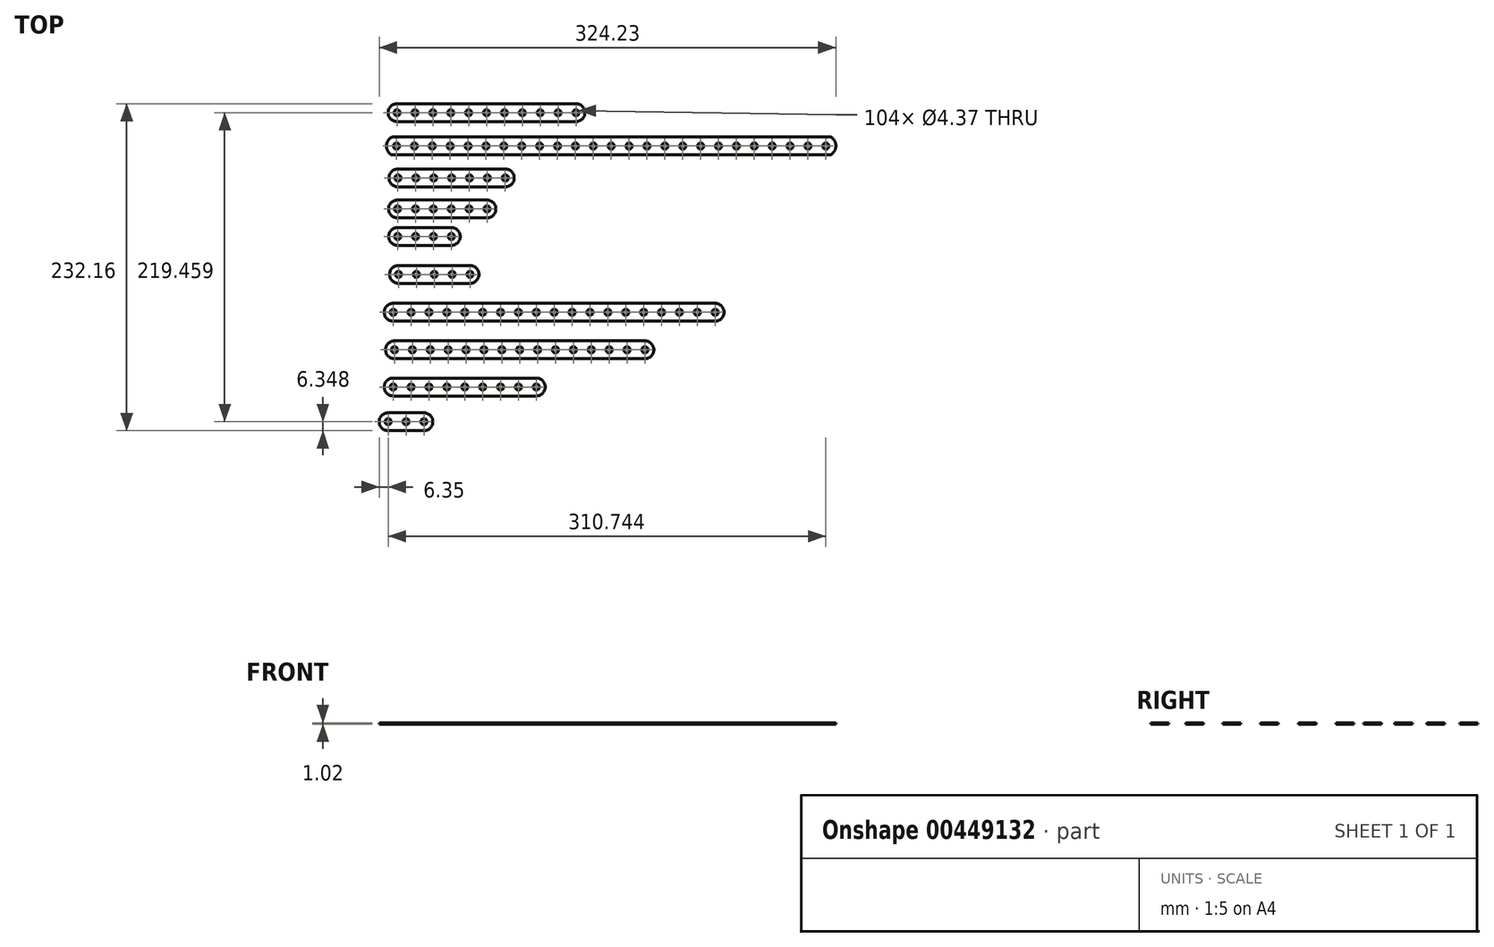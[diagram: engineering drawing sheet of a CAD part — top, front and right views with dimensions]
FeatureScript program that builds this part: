
annotation { "Feature Type Name" : "Feature", "Feature Type Description" : "" }
export const myFeature = defineFeature(function(context is Context, id is Id, definition is map)
    precondition{}
    {
        {
            var Q0;
            Q0=qCreatedBy(makeId("Top.planeOp"),FACE);
            var sketch = newSketch(context, id + "F0", { "sketchPlane" : qUnion([Q0])});
            skLineSegment(sketch, "E0", {"start": v(2.68, 70.57) * mm, "end": v(314.2, 70.57) * mm});
            skLineSegment(sketch, "E1", {"start": v(2.68, 57.87) * mm, "end": v(313.8, 57.87) * mm});
            skPoint(sketch, "E2", {"position": v(5.94, 71.36) * mm});
            skPoint(sketch, "E3", {"position": v(6.08, 56.78) * mm});
            skPoint(sketch, "E4", {"position": v(5.94, 64.22) * mm});
            skArc(sketch, "E5", {"start": v(2.68, 70.57) * mm, "mid": v(-1.2, 64.22) * mm, "end": v(2.68, 57.87) * mm});
            skPoint(sketch, "E6.orphan", {"position": v(0, 70.57) * mm});
            skPoint(sketch, "E7.orphan", {"position": v(5.94, 57.08) * mm});
            skPoint(sketch, "E8.orphan", {"position": v(0, 57.87) * mm});
            skArc(sketch, "E9", {"start": v(314.2, 70.57) * mm, "mid": v(317.88, 64.1) * mm, "end": v(313.8, 57.87) * mm});
            skPoint(sketch, "E10.orphan", {"position": v(310.74, 71.46) * mm});
            skPoint(sketch, "E11.orphan", {"position": v(310.74, 57.18) * mm});
            skCircle(sketch, "E12", {"center": v(5.94, 64.22) * mm, "radius": 2.18 * mm});
            skCircle(sketch, "E13.1.0.0", {"center": v(18.64, 64.22) * mm, "radius": 2.18 * mm});
            skCircle(sketch, "E13.2.0.0", {"center": v(31.34, 64.22) * mm, "radius": 2.18 * mm});
            skLineSegment(sketch, "E13.direction1", {"start": v(5.94, 64.22) * mm, "end": v(18.64, 64.22) * mm, "construction": true});
            skCircle(sketch, "E14.0.3.0", {"center": v(44.04, 64.22) * mm, "radius": 2.18 * mm});
            skCircle(sketch, "E14.0.4.0", {"center": v(56.74, 64.22) * mm, "radius": 2.18 * mm});
            skCircle(sketch, "E14.0.5.0", {"center": v(69.44, 64.22) * mm, "radius": 2.18 * mm});
            skCircle(sketch, "E14.0.6.0", {"center": v(82.14, 64.22) * mm, "radius": 2.18 * mm});
            skCircle(sketch, "E14.0.7.0", {"center": v(94.84, 64.22) * mm, "radius": 2.18 * mm});
            skCircle(sketch, "E14.0.8.0", {"center": v(107.54, 64.22) * mm, "radius": 2.18 * mm});
            skCircle(sketch, "E14.0.9.0", {"center": v(120.24, 64.22) * mm, "radius": 2.18 * mm});
            skCircle(sketch, "E14.0.10.0", {"center": v(132.94, 64.22) * mm, "radius": 2.18 * mm});
            skCircle(sketch, "E14.0.11.0", {"center": v(145.64, 64.22) * mm, "radius": 2.18 * mm});
            skCircle(sketch, "E14.0.12.0", {"center": v(158.34, 64.22) * mm, "radius": 2.18 * mm});
            skCircle(sketch, "E14.0.13.0", {"center": v(171.04, 64.22) * mm, "radius": 2.18 * mm});
            skCircle(sketch, "E14.0.14.0", {"center": v(183.74, 64.22) * mm, "radius": 2.18 * mm});
            skCircle(sketch, "E14.0.15.0", {"center": v(196.44, 64.22) * mm, "radius": 2.18 * mm});
            skCircle(sketch, "E14.0.16.0", {"center": v(209.14, 64.22) * mm, "radius": 2.18 * mm});
            skCircle(sketch, "E14.0.17.0", {"center": v(221.84, 64.22) * mm, "radius": 2.18 * mm});
            skCircle(sketch, "E14.0.18.0", {"center": v(234.54, 64.22) * mm, "radius": 2.18 * mm});
            skCircle(sketch, "E14.0.19.0", {"center": v(247.24, 64.22) * mm, "radius": 2.18 * mm});
            skCircle(sketch, "E14.0.20.0", {"center": v(259.94, 64.22) * mm, "radius": 2.18 * mm});
            skCircle(sketch, "E14.0.21.0", {"center": v(272.64, 64.22) * mm, "radius": 2.18 * mm});
            skCircle(sketch, "E14.0.22.0", {"center": v(285.34, 64.22) * mm, "radius": 2.18 * mm});
            skCircle(sketch, "E14.0.23.0", {"center": v(298.04, 64.22) * mm, "radius": 2.18 * mm});
            skCircle(sketch, "E14.0.24.0", {"center": v(310.74, 64.22) * mm, "radius": 2.18 * mm});
            skSolve(sketch);
        }
        {
            var Q0;
            Q0 = qSketchRegion(id + "F0", true);
            extrude(context, id + "F1", {"entities" : qUnion([Q0]), "depth" : 1.02 * mm});
        }
        {
            var Q0;
            Q0=qCreatedBy(makeId("Top.planeOp"),FACE);
            var sketch = newSketch(context, id + "F2", { "sketchPlane" : qUnion([Q0])});
            skLineSegment(sketch, "E15", {"start": v(6.35, 94.24) * mm, "end": v(133.35, 94.24) * mm});
            skLineSegment(sketch, "E16", {"start": v(6.35, 81.54) * mm, "end": v(133.35, 81.54) * mm});
            skArc(sketch, "E17", {"start": v(6.35, 94.24) * mm, "mid": v(0, 87.89) * mm, "end": v(6.35, 81.54) * mm});
            skArc(sketch, "E18", {"start": v(133.35, 94.24) * mm, "mid": v(139.7, 87.89) * mm, "end": v(133.35, 81.54) * mm});
            skCircle(sketch, "E19", {"center": v(6.35, 87.89) * mm, "radius": 2.18 * mm});
            skCircle(sketch, "E20.1.0.0", {"center": v(19.05, 87.89) * mm, "radius": 2.18 * mm});
            skCircle(sketch, "E20.2.0.0", {"center": v(31.75, 87.89) * mm, "radius": 2.18 * mm});
            skLineSegment(sketch, "E20.direction1", {"start": v(6.35, 87.89) * mm, "end": v(19.05, 87.89) * mm, "construction": true});
            skCircle(sketch, "E21.0.3.0", {"center": v(44.45, 87.89) * mm, "radius": 2.18 * mm});
            skCircle(sketch, "E21.0.4.0", {"center": v(57.15, 87.89) * mm, "radius": 2.18 * mm});
            skCircle(sketch, "E21.0.5.0", {"center": v(69.85, 87.89) * mm, "radius": 2.18 * mm});
            skCircle(sketch, "E21.0.6.0", {"center": v(82.55, 87.89) * mm, "radius": 2.18 * mm});
            skCircle(sketch, "E21.0.7.0", {"center": v(95.25, 87.89) * mm, "radius": 2.18 * mm});
            skCircle(sketch, "E21.0.8.0", {"center": v(107.95, 87.89) * mm, "radius": 2.18 * mm});
            skCircle(sketch, "E21.0.9.0", {"center": v(120.65, 87.89) * mm, "radius": 2.18 * mm});
            skCircle(sketch, "E21.0.10.0", {"center": v(133.35, 87.89) * mm, "radius": 2.18 * mm});
            skSolve(sketch);
        }
        {
            var Q0;
            Q0 = qSketchRegion(id + "F2", true);
            extrude(context, id + "F3", {"entities" : qUnion([Q0]), "depth" : 1.02 * mm});
        }
        {
            var Q0;
            Q0=qCreatedBy(makeId("Top.planeOp"),FACE);
            var sketch = newSketch(context, id + "F4", { "sketchPlane" : qUnion([Q0])});
            skLineSegment(sketch, "E22", {"start": v(6.95, 47.9) * mm, "end": v(83.15, 47.9) * mm});
            skLineSegment(sketch, "E23", {"start": v(6.95, 35.2) * mm, "end": v(83.15, 35.2) * mm});
            skArc(sketch, "E24", {"start": v(6.95, 47.9) * mm, "mid": v(0.6, 41.55) * mm, "end": v(6.95, 35.2) * mm});
            skArc(sketch, "E25", {"start": v(83.15, 47.9) * mm, "mid": v(89.5, 41.55) * mm, "end": v(83.15, 35.2) * mm});
            skCircle(sketch, "E26", {"center": v(6.95, 41.55) * mm, "radius": 2.18 * mm});
            skCircle(sketch, "E27.1.0.0", {"center": v(19.65, 41.55) * mm, "radius": 2.18 * mm});
            skCircle(sketch, "E27.2.0.0", {"center": v(32.35, 41.55) * mm, "radius": 2.18 * mm});
            skLineSegment(sketch, "E27.direction1", {"start": v(6.95, 41.55) * mm, "end": v(19.65, 41.55) * mm, "construction": true});
            skCircle(sketch, "E28.0.3.0", {"center": v(45.05, 41.55) * mm, "radius": 2.18 * mm});
            skCircle(sketch, "E28.0.4.0", {"center": v(57.75, 41.55) * mm, "radius": 2.18 * mm});
            skCircle(sketch, "E28.0.5.0", {"center": v(70.45, 41.55) * mm, "radius": 2.18 * mm});
            skCircle(sketch, "E28.0.6.0", {"center": v(83.15, 41.55) * mm, "radius": 2.18 * mm});
            skSolve(sketch);
        }
        {
            var Q0;
            Q0 = qSketchRegion(id + "F4", true);
            extrude(context, id + "F5", {"entities" : qUnion([Q0]), "depth" : 1.02 * mm});
        }
        {
            var Q0;
            Q0=qCreatedBy(makeId("Top.planeOp"),FACE);
            var sketch = newSketch(context, id + "F6", { "sketchPlane" : qUnion([Q0])});
            skLineSegment(sketch, "E29", {"start": v(6.67, 25.9) * mm, "end": v(70.17, 25.9) * mm});
            skLineSegment(sketch, "E30", {"start": v(6.67, 13.2) * mm, "end": v(70.17, 13.2) * mm});
            skArc(sketch, "E31", {"start": v(6.67, 25.9) * mm, "mid": v(0.32, 19.56) * mm, "end": v(6.67, 13.2) * mm});
            skArc(sketch, "E32", {"start": v(70.17, 25.9) * mm, "mid": v(76.52, 19.56) * mm, "end": v(70.17, 13.2) * mm});
            skCircle(sketch, "E33", {"center": v(6.67, 19.56) * mm, "radius": 2.18 * mm});
            skCircle(sketch, "E34.1.0.0", {"center": v(19.37, 19.56) * mm, "radius": 2.18 * mm});
            skCircle(sketch, "E34.2.0.0", {"center": v(32.07, 19.56) * mm, "radius": 2.18 * mm});
            skLineSegment(sketch, "E34.direction1", {"start": v(6.67, 19.56) * mm, "end": v(19.37, 19.56) * mm, "construction": true});
            skCircle(sketch, "E35.0.3.0", {"center": v(44.77, 19.56) * mm, "radius": 2.18 * mm});
            skCircle(sketch, "E35.0.4.0", {"center": v(57.47, 19.56) * mm, "radius": 2.18 * mm});
            skCircle(sketch, "E35.0.5.0", {"center": v(70.17, 19.56) * mm, "radius": 2.18 * mm});
            skSolve(sketch);
        }
        {
            var Q0;
            Q0 = qSketchRegion(id + "F6", true);
            extrude(context, id + "F7", {"entities" : qUnion([Q0]), "depth" : 1.02 * mm});
        }
        {
            var Q0;
            Q0=qCreatedBy(makeId("Top.planeOp"),FACE);
            var sketch = newSketch(context, id + "F8", { "sketchPlane" : qUnion([Q0])});
            skLineSegment(sketch, "E36", {"start": v(7.36, -20.6) * mm, "end": v(58.16, -20.6) * mm});
            skLineSegment(sketch, "E37", {"start": v(7.36, -33.3) * mm, "end": v(58.16, -33.3) * mm});
            skArc(sketch, "E38", {"start": v(7.36, -20.6) * mm, "mid": v(1, -26.96) * mm, "end": v(7.36, -33.3) * mm});
            skArc(sketch, "E39", {"start": v(58.16, -20.6) * mm, "mid": v(64.5, -26.96) * mm, "end": v(58.16, -33.3) * mm});
            skCircle(sketch, "E40", {"center": v(7.36, -26.96) * mm, "radius": 2.18 * mm});
            skCircle(sketch, "E41.1.0.0", {"center": v(20.06, -26.96) * mm, "radius": 2.18 * mm});
            skCircle(sketch, "E41.2.0.0", {"center": v(32.76, -26.96) * mm, "radius": 2.18 * mm});
            skLineSegment(sketch, "E41.direction1", {"start": v(7.36, -26.96) * mm, "end": v(20.06, -26.96) * mm, "construction": true});
            skCircle(sketch, "E42.0.3.0", {"center": v(45.46, -26.96) * mm, "radius": 2.18 * mm});
            skCircle(sketch, "E42.0.4.0", {"center": v(58.16, -26.96) * mm, "radius": 2.18 * mm});
            skSolve(sketch);
        }
        {
            var Q0;
            Q0 = qSketchRegion(id + "F8", true);
            extrude(context, id + "F9", {"entities" : qUnion([Q0]), "depth" : 1.02 * mm});
        }
        {
            var Q0;
            Q0=qCreatedBy(makeId("Top.planeOp"),FACE);
            var sketch = newSketch(context, id + "F10", { "sketchPlane" : qUnion([Q0])});
            skLineSegment(sketch, "E43", {"start": v(6.76, 6.32) * mm, "end": v(44.86, 6.32) * mm});
            skLineSegment(sketch, "E44", {"start": v(6.76, -6.38) * mm, "end": v(44.86, -6.38) * mm});
            skArc(sketch, "E45", {"start": v(6.76, 6.32) * mm, "mid": v(0.41, -0.03) * mm, "end": v(6.76, -6.38) * mm});
            skArc(sketch, "E46", {"start": v(44.86, 6.32) * mm, "mid": v(51.21, -0.03) * mm, "end": v(44.86, -6.38) * mm});
            skCircle(sketch, "E47", {"center": v(6.76, -0.03) * mm, "radius": 2.18 * mm});
            skCircle(sketch, "E48.1.0.0", {"center": v(19.46, -0.03) * mm, "radius": 2.18 * mm});
            skCircle(sketch, "E48.2.0.0", {"center": v(32.16, -0.03) * mm, "radius": 2.18 * mm});
            skLineSegment(sketch, "E48.direction1", {"start": v(6.76, -0.03) * mm, "end": v(19.46, -0.03) * mm, "construction": true});
            skCircle(sketch, "E49.0.3.0", {"center": v(44.86, -0.03) * mm, "radius": 2.18 * mm});
            skSolve(sketch);
        }
        {
            var Q0;
            Q0 = qSketchRegion(id + "F10", true);
            extrude(context, id + "F11", {"entities" : qUnion([Q0]), "depth" : 1.02 * mm});
        }
        {
            var Q0;
            Q0=qCreatedBy(makeId("Top.planeOp"),FACE);
            var sketch = newSketch(context, id + "F12", { "sketchPlane" : qUnion([Q0])});
            skLineSegment(sketch, "E50", {"start": v(3.57, -47.5) * mm, "end": v(232.17, -47.5) * mm});
            skLineSegment(sketch, "E51", {"start": v(3.57, -60.2) * mm, "end": v(232.17, -60.2) * mm});
            skArc(sketch, "E52", {"start": v(3.57, -47.5) * mm, "mid": v(-2.78, -53.85) * mm, "end": v(3.57, -60.2) * mm});
            skArc(sketch, "E53", {"start": v(232.17, -47.5) * mm, "mid": v(238.52, -53.85) * mm, "end": v(232.17, -60.2) * mm});
            skCircle(sketch, "E54", {"center": v(3.57, -53.85) * mm, "radius": 2.18 * mm});
            skCircle(sketch, "E55.1.0.0", {"center": v(16.27, -53.85) * mm, "radius": 2.18 * mm});
            skCircle(sketch, "E55.2.0.0", {"center": v(28.97, -53.85) * mm, "radius": 2.18 * mm});
            skLineSegment(sketch, "E55.direction1", {"start": v(3.57, -53.85) * mm, "end": v(16.27, -53.85) * mm, "construction": true});
            skCircle(sketch, "E56.0.3.0", {"center": v(41.67, -53.85) * mm, "radius": 2.18 * mm});
            skCircle(sketch, "E56.0.4.0", {"center": v(54.37, -53.85) * mm, "radius": 2.18 * mm});
            skCircle(sketch, "E56.0.5.0", {"center": v(67.07, -53.85) * mm, "radius": 2.18 * mm});
            skCircle(sketch, "E56.0.6.0", {"center": v(79.77, -53.85) * mm, "radius": 2.18 * mm});
            skCircle(sketch, "E56.0.7.0", {"center": v(92.47, -53.85) * mm, "radius": 2.18 * mm});
            skCircle(sketch, "E56.0.8.0", {"center": v(105.17, -53.85) * mm, "radius": 2.18 * mm});
            skCircle(sketch, "E56.0.9.0", {"center": v(117.87, -53.85) * mm, "radius": 2.18 * mm});
            skCircle(sketch, "E56.0.10.0", {"center": v(130.57, -53.85) * mm, "radius": 2.18 * mm});
            skCircle(sketch, "E57.0.11.0", {"center": v(143.27, -53.85) * mm, "radius": 2.18 * mm});
            skCircle(sketch, "E57.0.12.0", {"center": v(155.97, -53.85) * mm, "radius": 2.18 * mm});
            skCircle(sketch, "E57.0.13.0", {"center": v(168.67, -53.85) * mm, "radius": 2.18 * mm});
            skCircle(sketch, "E57.0.14.0", {"center": v(181.37, -53.85) * mm, "radius": 2.18 * mm});
            skCircle(sketch, "E57.0.15.0", {"center": v(194.07, -53.85) * mm, "radius": 2.18 * mm});
            skCircle(sketch, "E57.0.16.0", {"center": v(206.77, -53.85) * mm, "radius": 2.18 * mm});
            skCircle(sketch, "E57.0.17.0", {"center": v(219.47, -53.85) * mm, "radius": 2.18 * mm});
            skCircle(sketch, "E57.0.18.0", {"center": v(232.17, -53.85) * mm, "radius": 2.18 * mm});
            skSolve(sketch);
        }
        {
            var Q0;
            Q0 = qSketchRegion(id + "F12", true);
            extrude(context, id + "F13", {"entities" : qUnion([Q0]), "depth" : 1.02 * mm});
        }
        {
            var Q0;
            Q0=qCreatedBy(makeId("Top.planeOp"),FACE);
            var sketch = newSketch(context, id + "F14", { "sketchPlane" : qUnion([Q0])});
            skLineSegment(sketch, "E58", {"start": v(4.5, -74.17) * mm, "end": v(182.3, -74.17) * mm});
            skLineSegment(sketch, "E59", {"start": v(4.5, -86.87) * mm, "end": v(182.3, -86.87) * mm});
            skArc(sketch, "E60", {"start": v(4.5, -74.17) * mm, "mid": v(-1.85, -80.52) * mm, "end": v(4.5, -86.87) * mm});
            skArc(sketch, "E61", {"start": v(182.3, -74.17) * mm, "mid": v(188.65, -80.52) * mm, "end": v(182.3, -86.87) * mm});
            skCircle(sketch, "E62", {"center": v(4.5, -80.52) * mm, "radius": 2.18 * mm});
            skCircle(sketch, "E63.1.0.0", {"center": v(17.2, -80.52) * mm, "radius": 2.18 * mm});
            skCircle(sketch, "E63.2.0.0", {"center": v(29.9, -80.52) * mm, "radius": 2.18 * mm});
            skLineSegment(sketch, "E63.direction1", {"start": v(4.5, -80.52) * mm, "end": v(17.2, -80.52) * mm, "construction": true});
            skCircle(sketch, "E64.0.3.0", {"center": v(42.6, -80.52) * mm, "radius": 2.18 * mm});
            skCircle(sketch, "E64.0.4.0", {"center": v(55.3, -80.52) * mm, "radius": 2.18 * mm});
            skCircle(sketch, "E64.0.5.0", {"center": v(68, -80.52) * mm, "radius": 2.18 * mm});
            skCircle(sketch, "E64.0.6.0", {"center": v(80.7, -80.52) * mm, "radius": 2.18 * mm});
            skCircle(sketch, "E64.0.7.0", {"center": v(93.4, -80.52) * mm, "radius": 2.18 * mm});
            skCircle(sketch, "E64.0.8.0", {"center": v(106.1, -80.52) * mm, "radius": 2.18 * mm});
            skCircle(sketch, "E64.0.9.0", {"center": v(118.8, -80.52) * mm, "radius": 2.18 * mm});
            skCircle(sketch, "E64.0.10.0", {"center": v(131.5, -80.52) * mm, "radius": 2.18 * mm});
            skCircle(sketch, "E65.0.11.0", {"center": v(144.2, -80.52) * mm, "radius": 2.18 * mm});
            skCircle(sketch, "E65.0.12.0", {"center": v(156.9, -80.52) * mm, "radius": 2.18 * mm});
            skCircle(sketch, "E65.0.13.0", {"center": v(169.6, -80.52) * mm, "radius": 2.18 * mm});
            skCircle(sketch, "E65.0.14.0", {"center": v(182.3, -80.52) * mm, "radius": 2.18 * mm});
            skSolve(sketch);
        }
        {
            var Q0;
            Q0 = qSketchRegion(id + "F14", true);
            extrude(context, id + "F15", {"entities" : qUnion([Q0]), "depth" : 1.02 * mm});
        }
        {
            var Q0;
            Q0=qCreatedBy(makeId("Top.planeOp"),FACE);
            var sketch = newSketch(context, id + "F16", { "sketchPlane" : qUnion([Q0])});
            skLineSegment(sketch, "E66", {"start": v(3.57, -100.58) * mm, "end": v(105.17, -100.58) * mm});
            skLineSegment(sketch, "E67", {"start": v(3.57, -113.28) * mm, "end": v(105.17, -113.28) * mm});
            skArc(sketch, "E68", {"start": v(3.57, -100.58) * mm, "mid": v(-2.78, -106.93) * mm, "end": v(3.57, -113.28) * mm});
            skArc(sketch, "E69", {"start": v(105.17, -100.58) * mm, "mid": v(111.52, -106.93) * mm, "end": v(105.17, -113.28) * mm});
            skCircle(sketch, "E70", {"center": v(3.57, -106.93) * mm, "radius": 2.18 * mm});
            skCircle(sketch, "E71.1.0.0", {"center": v(16.27, -106.93) * mm, "radius": 2.18 * mm});
            skCircle(sketch, "E71.2.0.0", {"center": v(28.97, -106.93) * mm, "radius": 2.18 * mm});
            skLineSegment(sketch, "E71.direction1", {"start": v(3.57, -106.93) * mm, "end": v(16.27, -106.93) * mm, "construction": true});
            skCircle(sketch, "E72.0.3.0", {"center": v(41.67, -106.93) * mm, "radius": 2.18 * mm});
            skCircle(sketch, "E72.0.4.0", {"center": v(54.37, -106.93) * mm, "radius": 2.18 * mm});
            skCircle(sketch, "E72.0.5.0", {"center": v(67.07, -106.93) * mm, "radius": 2.18 * mm});
            skCircle(sketch, "E72.0.6.0", {"center": v(79.77, -106.93) * mm, "radius": 2.18 * mm});
            skCircle(sketch, "E72.0.7.0", {"center": v(92.47, -106.93) * mm, "radius": 2.18 * mm});
            skCircle(sketch, "E72.0.8.0", {"center": v(105.17, -106.93) * mm, "radius": 2.18 * mm});
            skSolve(sketch);
        }
        {
            var Q0;
            Q0 = qSketchRegion(id + "F16", true);
            extrude(context, id + "F17", {"entities" : qUnion([Q0]), "depth" : 1.02 * mm});
        }
        {
            var Q0;
            Q0=qCreatedBy(makeId("Top.planeOp"),FACE);
            var sketch = newSketch(context, id + "F18", { "sketchPlane" : qUnion([Q0])});
            skLineSegment(sketch, "E73", {"start": v(0, -125.22) * mm, "end": v(25.4, -125.22) * mm});
            skLineSegment(sketch, "E74", {"start": v(0, -137.92) * mm, "end": v(25.4, -137.92) * mm});
            skArc(sketch, "E75", {"start": v(0, -125.22) * mm, "mid": v(-6.35, -131.57) * mm, "end": v(0, -137.92) * mm});
            skArc(sketch, "E76", {"start": v(25.4, -125.22) * mm, "mid": v(31.75, -131.57) * mm, "end": v(25.4, -137.92) * mm});
            skCircle(sketch, "E77", {"center": v(0, -131.57) * mm, "radius": 2.18 * mm});
            skCircle(sketch, "E78.1.0.0", {"center": v(12.7, -131.57) * mm, "radius": 2.18 * mm});
            skCircle(sketch, "E78.2.0.0", {"center": v(25.4, -131.57) * mm, "radius": 2.18 * mm});
            skLineSegment(sketch, "E78.direction1", {"start": v(0, -131.57) * mm, "end": v(12.7, -131.57) * mm, "construction": true});
            skSolve(sketch);
        }
        {
            var Q0;
            Q0 = qSketchRegion(id + "F18", true);
            extrude(context, id + "F19", {"entities" : qUnion([Q0]), "depth" : 1.02 * mm});
        }
    });
